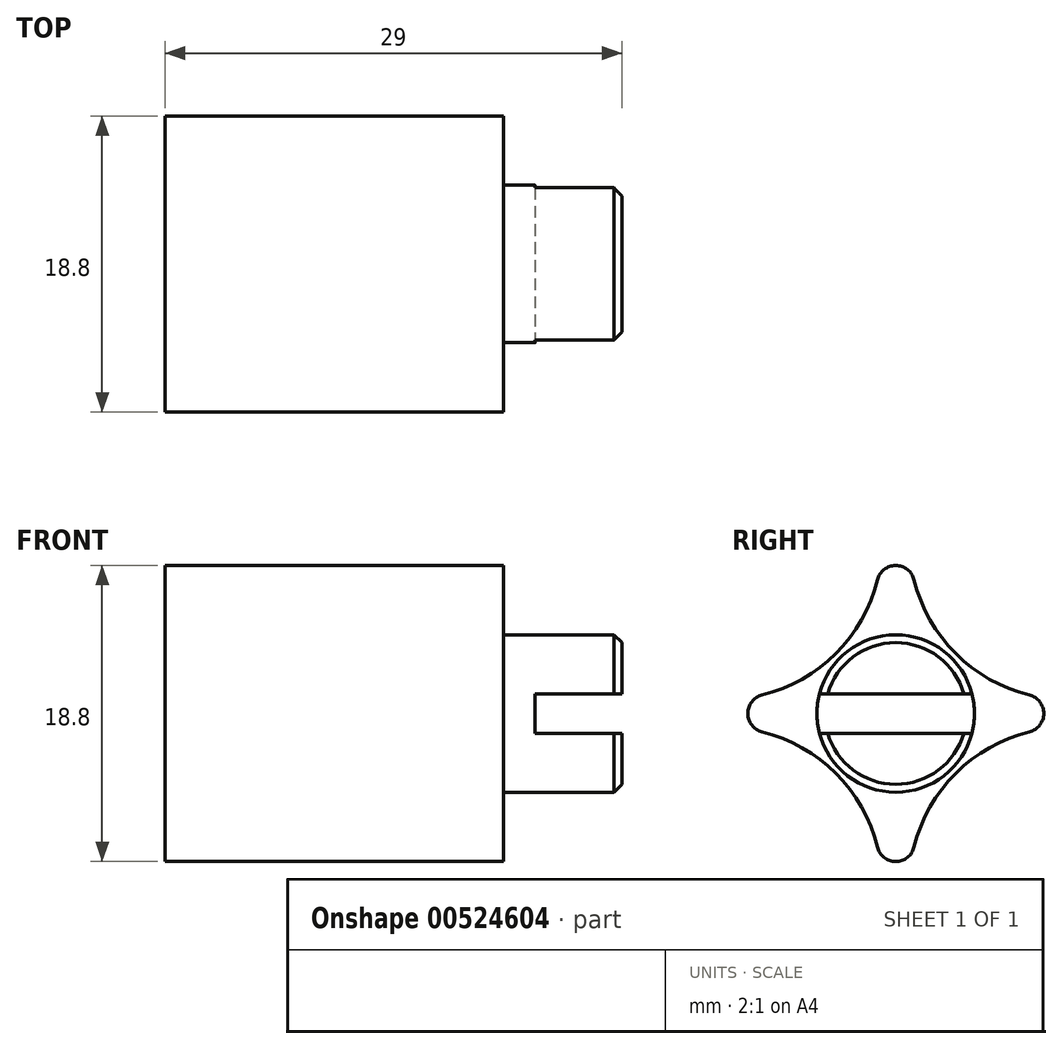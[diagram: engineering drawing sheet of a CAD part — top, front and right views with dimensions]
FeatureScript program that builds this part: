
annotation { "Feature Type Name" : "Feature", "Feature Type Description" : "" }
export const myFeature = defineFeature(function(context is Context, id is Id, definition is map)
    precondition{}
    {
        {
            var Q0;
            Q0=qCreatedBy(makeId("Right.planeOp"),FACE);
            var sketch = newSketch(context, id + "F0", { "sketchPlane" : qUnion([Q0])});
            skCircle(sketch, "E0", {"center": v(0, 0) * mm, "radius": 9.4 * mm, "construction": true});
            skCircle(sketch, "E1", {"center": v(0, 8.2) * mm, "radius": 1.2 * mm});
            skCircle(sketch, "E2", {"center": v(8.2, 0) * mm, "radius": 1.2 * mm});
            skArc(sketch, "E3", {"start": v(1.17, 8.49) * mm, "mid": v(3.8, 3.8) * mm, "end": v(8.49, 1.17) * mm});
            skCircle(sketch, "E4", {"center": v(-8.2, 0) * mm, "radius": 1.2 * mm});
            skCircle(sketch, "E5", {"center": v(0, -8.2) * mm, "radius": 1.2 * mm});
            skArc(sketch, "E6.1.0", {"start": v(-8.49, 1.17) * mm, "mid": v(-3.8, 3.8) * mm, "end": v(-1.17, 8.49) * mm});
            skArc(sketch, "E6.2.0", {"start": v(-1.17, -8.49) * mm, "mid": v(-3.8, -3.8) * mm, "end": v(-8.49, -1.17) * mm});
            skArc(sketch, "E6.3.0", {"start": v(8.49, -1.17) * mm, "mid": v(3.8, -3.8) * mm, "end": v(1.17, -8.49) * mm});
            skSolve(sketch);
        }
        {
            var Q0;
            Q0 = qSketchRegion(id + "F0", true);
            extrude(context, id + "F1", {"entities" : qUnion([Q0]), "depth" : 21.5 * mm, "offsetDistance" : 25 * mm});
        }
        {
            var Q0;
            Q0=makeQuery(id+"F1.opExtrude","CAP_FACE",FACE,{"disambiguationData":[OSD([sQuery(id+"F0.wireOp",EDGE,"E1"),sQuery(id+"F0.wireOp",EDGE,"E2"),sQuery(id+"F0.wireOp",EDGE,"E3"),sQuery(id+"F0.wireOp",EDGE,"E4"),sQuery(id+"F0.wireOp",EDGE,"E5"),sQuery(id+"F0.wireOp",EDGE,"E6.1.0"),sQuery(id+"F0.wireOp",EDGE,"E6.2.0"),sQuery(id+"F0.wireOp",EDGE,"E6.3.0")])],"isStart":false});
            var sketch = newSketch(context, id + "F2", { "sketchPlane" : qUnion([Q0])});
            skCircle(sketch, "E7", {"center": v(0, 0) * mm, "radius": 5 * mm});
            skSolve(sketch);
        }
        {
            var Q0;
            Q0 = qSketchRegion(id + "F2", true);
            extrude(context, id + "F3", {"entities" : qUnion([Q0]), "operationType" : NewBodyOperationType.ADD, "depth" : (29 - 21.5) * mm, "offsetDistance" : 25 * mm});
        }
        {
            var Q0;
            Q0=makeQuery(id+"F3.opExtrude","CAP_EDGE",EDGE,{"disambiguationData":[OSD([sQuery(id+"F2.wireOp",EDGE,"E7")])],"isStart":false});
            chamfer(context, id + "F4", {"entities" : qUnion([Q0]), "width" : 0.5 * mm, "tangentPropagation" : true});
        }
        {
            var Q0;
            Q0=makeQuery(id+"F3.opExtrude","CAP_FACE",FACE,{"disambiguationData":[OSD([sQuery(id+"F2.wireOp",EDGE,"E7")])],"isStart":false});
            var sketch = newSketch(context, id + "F5", { "sketchPlane" : qUnion([Q0])});
            skCircle(sketch, "E8.0", {"center": v(0, 0) * mm, "radius": 5 * mm});
            skLineSegment(sketch, "E9.bottom", {"start": v(4.84, 1.25) * mm, "end": v(-4.84, 1.25) * mm});
            skLineSegment(sketch, "E9.top", {"start": v(4.84, -1.25) * mm, "end": v(-4.84, -1.25) * mm});
            skSolve(sketch);
        }
        {
            var Q0;
            {var subQ0=sQuery(id+"F5.wireOp",EDGE,"E9.bottom");var subQ1=sQuery(id+"F2.wireOp",EDGE,"E7");var subQ2=makeQuery(id+"F4.opChamfer","BLEND_EDGE",EDGE,{"blendedFrom":[makeQuery(id+"F3.opExtrude","CAP_EDGE",EDGE,{"disambiguationData":[OSD([subQ1])],"isStart":false}),makeQuery(id+"F3.opExtrude","CAP_FACE",FACE,{"disambiguationData":[OSD([subQ1])],"isStart":false})],"blendedInto":[makeQuery(id+"F3.opExtrude","CAP_FACE",FACE,{"disambiguationData":[OSD([subQ1])],"isStart":false})]});var subQ3=makeQuery(id+"F5.imprint","INTERSECT",VERTEX,{"disambiguationData":[OD(0.0)],"derivedFrom":[subQ2,subQ0]});Q0=makeQuery(id+"F5.imprint","IMPRINT",FACE,{"disambiguationData":[TD([[makeQuery(id+"F5.imprint","IMPRINT",EDGE,{"disambiguationData":[TD([[subQ3,-1.0]])],"derivedFrom":subQ0}),1.0]])]});}
            var Q1;
            {var subQ0=sQuery(id+"F5.wireOp",EDGE,"E9.bottom");var subQ1=sQuery(id+"F5.wireOp",EDGE,"E8.0");var subQ2=makeQuery(id+"F5.imprint","INTERSECT",VERTEX,{"disambiguationData":[OD(1.0)],"derivedFrom":[subQ1,subQ0]});Q1=makeQuery(id+"F5.imprint","IMPRINT",FACE,{"disambiguationData":[TD([[makeQuery(id+"F5.imprint","IMPRINT",EDGE,{"disambiguationData":[TD([[subQ2,-1.0]])],"derivedFrom":subQ1}),1.0]])]});}
            var Q2;
            {var subQ0=sQuery(id+"F5.wireOp",EDGE,"E9.bottom");var subQ1=sQuery(id+"F5.wireOp",EDGE,"E8.0");var subQ2=makeQuery(id+"F5.imprint","INTERSECT",VERTEX,{"disambiguationData":[OD(0.0)],"derivedFrom":[subQ1,subQ0]});Q2=makeQuery(id+"F5.imprint","IMPRINT",FACE,{"disambiguationData":[TD([[makeQuery(id+"F5.imprint","IMPRINT",EDGE,{"disambiguationData":[TD([[subQ2,1.0]])],"derivedFrom":subQ1}),1.0]])]});}
            extrude(context, id + "F6", {"entities" : qUnion([Q0, Q1, Q2]), "operationType" : NewBodyOperationType.REMOVE, "oppositeDirection" : true, "depth" : 5.5 * mm, "offsetDistance" : 25 * mm});
        }
    });
